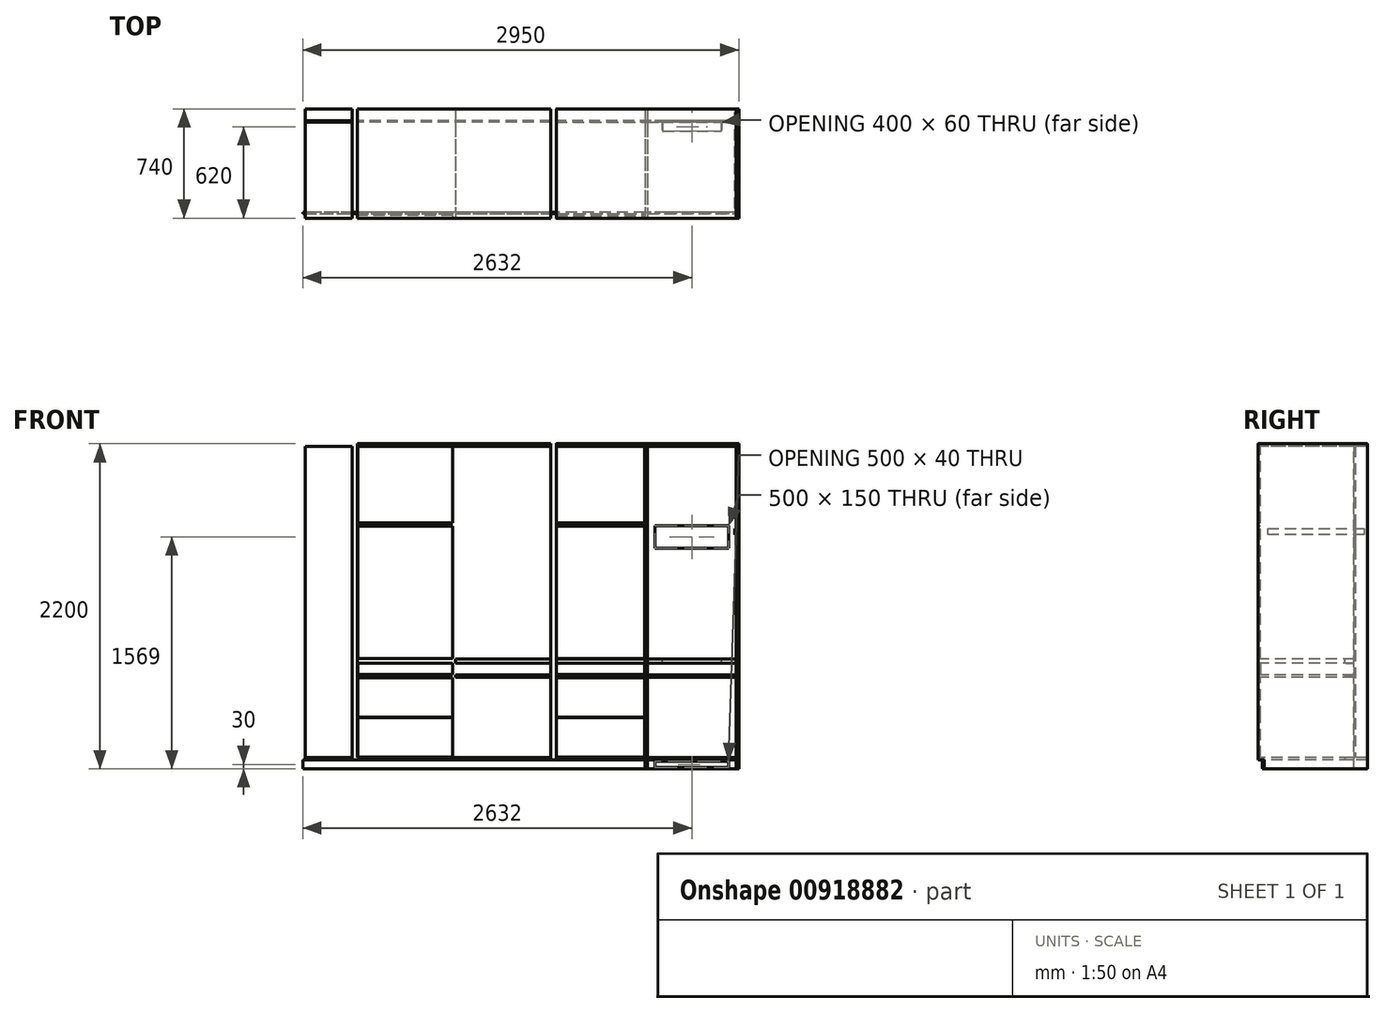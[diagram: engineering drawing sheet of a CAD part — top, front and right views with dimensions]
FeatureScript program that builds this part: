
annotation { "Feature Type Name" : "Feature", "Feature Type Description" : "" }
export const myFeature = defineFeature(function(context is Context, id is Id, definition is map)
    precondition{}
    {
        {
            var Q0;
            Q0=qCreatedBy(makeId("Front.planeOp"),FACE);
            var sketch = newSketch(context, id + "F0", { "sketchPlane" : qUnion([Q0])});
            skLineSegment(sketch, "E0.right", {"start": v(2950, 0) * mm, "end": v(2950, 2200) * mm});
            skLineSegment(sketch, "E1", {"start": v(1714, 2200) * mm, "end": v(1714, 0) * mm});
            skLineSegment(sketch, "E2", {"start": v(2332, 0) * mm, "end": v(2332, 2182) * mm});
            skLineSegment(sketch, "E3", {"start": v(1696, 0) * mm, "end": v(1696, 2200) * mm});
            skLineSegment(sketch, "E4", {"start": v(2932, 0) * mm, "end": v(2932, 2200) * mm});
            skLineSegment(sketch, "E5", {"start": v(2314, 0) * mm, "end": v(2314, 2182) * mm});
            skLineSegment(sketch, "E6", {"start": v(2932, 2200) * mm, "end": v(2950, 2200) * mm});
            skLineSegment(sketch, "E7", {"start": v(2932, 2200) * mm, "end": v(1714, 2200) * mm});
            skLineSegment(sketch, "E8", {"start": v(1714, 2182) * mm, "end": v(2932, 2182) * mm});
            skLineSegment(sketch, "E9", {"start": v(1714, 2200) * mm, "end": v(1696, 2200) * mm});
            skLineSegment(sketch, "E10", {"start": v(1714, 0) * mm, "end": v(1696, 0) * mm});
            skLineSegment(sketch, "E11", {"start": v(2932, 0) * mm, "end": v(2950, 0) * mm});
            skLineSegment(sketch, "E12", {"start": v(1714, 744) * mm, "end": v(2314, 744) * mm});
            skLineSegment(sketch, "E13", {"start": v(1714, 716) * mm, "end": v(2314, 716) * mm});
            skLineSegment(sketch, "E14", {"start": v(1714, 1662) * mm, "end": v(2314, 1662) * mm});
            skLineSegment(sketch, "E15", {"start": v(2932, 1644) * mm, "end": v(2332, 1644) * mm});
            skLineSegment(sketch, "E16.MirrorCS", {"start": v(1678, 2200) * mm, "end": v(1678, 0) * mm});
            skLineSegment(sketch, "E17.MirrorCS", {"start": v(1678, 2182) * mm, "end": v(370, 2182) * mm});
            skLineSegment(sketch, "E18.MirrorCS", {"start": v(370, 2200) * mm, "end": v(1678, 2200) * mm});
            skLineSegment(sketch, "E19.MirrorCS", {"start": v(1015, 0) * mm, "end": v(1015, 2182) * mm});
            skLineSegment(sketch, "E20.MirrorCS", {"start": v(1033, 0) * mm, "end": v(1033, 2182) * mm});
            skLineSegment(sketch, "E21.MirrorCS", {"start": v(370, 0) * mm, "end": v(370, 2200) * mm});
            skLineSegment(sketch, "E22.MirrorCS", {"start": v(1678, 0) * mm, "end": v(1696, 0) * mm});
            skLineSegment(sketch, "E23.MirrorCS", {"start": v(1678, 2200) * mm, "end": v(1696, 2200) * mm});
            skLineSegment(sketch, "E24", {"start": v(2932, 618) * mm, "end": v(2332, 618) * mm});
            skLineSegment(sketch, "E25", {"start": v(2332, 636) * mm, "end": v(2932, 636) * mm});
            skLineSegment(sketch, "E26", {"start": v(2314, 636) * mm, "end": v(1714, 636) * mm});
            skLineSegment(sketch, "E27", {"start": v(1714, 618) * mm, "end": v(2314, 618) * mm});
            skLineSegment(sketch, "E28", {"start": v(1678, 1644) * mm, "end": v(1033, 1644) * mm});
            skLineSegment(sketch, "E29", {"start": v(1678, 1662) * mm, "end": v(1033, 1662) * mm});
            skLineSegment(sketch, "E30", {"start": v(1678, 716) * mm, "end": v(1033, 716) * mm});
            skLineSegment(sketch, "E31", {"start": v(1015, 716) * mm, "end": v(370, 716) * mm});
            skLineSegment(sketch, "E32", {"start": v(1678, 618) * mm, "end": v(1033, 618) * mm});
            skLineSegment(sketch, "E33", {"start": v(1015, 618) * mm, "end": v(370, 618) * mm});
            skLineSegment(sketch, "E34", {"start": v(1678, 744) * mm, "end": v(1033, 744) * mm});
            skLineSegment(sketch, "E35", {"start": v(1015, 744) * mm, "end": v(370, 744) * mm});
            skLineSegment(sketch, "E36", {"start": v(1678, 636) * mm, "end": v(1033, 636) * mm});
            skLineSegment(sketch, "E37", {"start": v(1015, 636) * mm, "end": v(370, 636) * mm});
            skLineSegment(sketch, "E38", {"start": v(352, 2200) * mm, "end": v(352, 10) * mm});
            skLineSegment(sketch, "E39", {"start": v(334, 10) * mm, "end": v(334, 2200) * mm});
            skLineSegment(sketch, "E40", {"start": v(0, 2200) * mm, "end": v(334, 2200) * mm});
            skLineSegment(sketch, "E41", {"start": v(334, 2182) * mm, "end": v(18, 2182) * mm});
            skLineSegment(sketch, "E42", {"start": v(334, 2200) * mm, "end": v(352, 2200) * mm});
            skLineSegment(sketch, "E43", {"start": v(352, 10) * mm, "end": v(334, 10) * mm});
            skLineSegment(sketch, "E44", {"start": v(352, 10) * mm, "end": v(370, 10) * mm});
            skLineSegment(sketch, "E45", {"start": v(18, 2200) * mm, "end": v(18, 0) * mm});
            skLineSegment(sketch, "E46", {"start": v(0, 2200) * mm, "end": v(0, 0) * mm});
            skLineSegment(sketch, "E47.trimOffspring", {"start": v(2332, 744) * mm, "end": v(2932, 744) * mm});
            skLineSegment(sketch, "E48.trimOffspring", {"start": v(2332, 1662) * mm, "end": v(2932, 1662) * mm});
            skLineSegment(sketch, "E49.trimOffspring", {"start": v(2314, 1644) * mm, "end": v(1714, 1644) * mm});
            skLineSegment(sketch, "E50.trimOffspring", {"start": v(1015, 1662) * mm, "end": v(370, 1662) * mm});
            skLineSegment(sketch, "E51.trimOffspring", {"start": v(1015, 1644) * mm, "end": v(370, 1644) * mm});
            skLineSegment(sketch, "E52", {"start": v(2332, 716) * mm, "end": v(2932, 716) * mm});
            skLineSegment(sketch, "E53", {"start": v(2314, 0) * mm, "end": v(2332, 0) * mm});
            skLineSegment(sketch, "E54", {"start": v(1015, 0) * mm, "end": v(1033, 0) * mm});
            skLineSegment(sketch, "E55", {"start": v(0, 0) * mm, "end": v(18, 0) * mm});
            skLineSegment(sketch, "E56", {"start": v(2932, 60) * mm, "end": v(2332, 60) * mm});
            skLineSegment(sketch, "E57", {"start": v(2932, 78) * mm, "end": v(2332, 78) * mm});
            skLineSegment(sketch, "E58", {"start": v(2314, 60) * mm, "end": v(1714, 60) * mm});
            skLineSegment(sketch, "E59", {"start": v(2314, 78) * mm, "end": v(1714, 78) * mm});
            skLineSegment(sketch, "E60", {"start": v(1678, 78) * mm, "end": v(1033, 78) * mm});
            skLineSegment(sketch, "E61", {"start": v(1678, 60) * mm, "end": v(1033, 60) * mm});
            skLineSegment(sketch, "E62", {"start": v(1015, 78) * mm, "end": v(370, 78) * mm});
            skLineSegment(sketch, "E63", {"start": v(1015, 60) * mm, "end": v(370, 60) * mm});
            skLineSegment(sketch, "E64", {"start": v(334, 78) * mm, "end": v(18, 78) * mm});
            skLineSegment(sketch, "E65", {"start": v(334, 60) * mm, "end": v(18, 60) * mm});
            skLineSegment(sketch, "E66", {"start": v(352, 2200) * mm, "end": v(370, 2200) * mm});
            skSolve(sketch);
        }
        {
            var Q0;
            Q0=makeQuery(id+"F0.imprint","IMPRINT",FACE,{"disambiguationData":[TD([[makeQuery(id+"F0.imprint","IMPRINT",EDGE,{"derivedFrom":sQuery(id+"F0.wireOp",EDGE,"E0.right")}),1.0]])]});
            extrude(context, id + "F1", {"entities" : qUnion([Q0]), "oppositeDirection" : true, "depth" : 740 * mm, "offsetDistance" : 25 * mm});
        }
        {
            var Q0;
            {var subQ0=sQuery(id+"F0.wireOp",EDGE,"E24");Q0=makeQuery(id+"F0.imprint","IMPRINT",FACE,{"disambiguationData":[TD([[makeQuery(id+"F0.imprint","IMPRINT",EDGE,{"derivedFrom":subQ0}),-1.0]])]});}
            extrude(context, id + "F2", {"entities" : qUnion([Q0]), "oppositeDirection" : true, "depth" : 650 * mm, "offsetDistance" : 25 * mm});
        }
        {
            var Q0;
            {var subQ0=sQuery(id+"F0.wireOp",EDGE,"E47.trimOffspring");Q0=makeQuery(id+"F0.imprint","IMPRINT",FACE,{"disambiguationData":[TD([[makeQuery(id+"F0.imprint","IMPRINT",EDGE,{"derivedFrom":subQ0}),-1.0]])]});}
            extrude(context, id + "F3", {"entities" : qUnion([Q0]), "oppositeDirection" : true, "depth" : 650 * mm, "offsetDistance" : 25 * mm});
        }
        {
            var Q0;
            {var subQ4=sQuery(id+"F0.wireOp",EDGE,"E7");Q0=makeQuery(id+"F0.imprint","IMPRINT",FACE,{"disambiguationData":[TD([[makeQuery(id+"F0.imprint","IMPRINT",EDGE,{"derivedFrom":subQ4}),1.0]])]});}
            extrude(context, id + "F4", {"entities" : qUnion([Q0]), "oppositeDirection" : true, "depth" : 740 * mm, "offsetDistance" : 25 * mm});
        }
        {
            var Q0;
            {var subQ4=sQuery(id+"F0.wireOp",EDGE,"Y9ucpfED-vLSd-DeHG-6LsV-7PyXNKgOYs4r");var subQ7=sQuery(id+"F0.wireOp",EDGE,"E2");var subQ12=makeQuery(id+"F0.imprint","INTERSECT",VERTEX,{"derivedFrom":[subQ7,subQ4]});Q0=makeQuery(id+"F0.imprint","IMPRINT",FACE,{"disambiguationData":[TD([[makeQuery(id+"F0.imprint","IMPRINT",EDGE,{"disambiguationData":[TD([[subQ12,-1.0]])],"derivedFrom":subQ7}),1.0]])]});}
            extrude(context, id + "F5", {"entities" : qUnion([Q0]), "oppositeDirection" : true, "depth" : 650 * mm, "offsetDistance" : 25 * mm});
        }
        {
            var Q0;
            Q0=makeQuery(id+"F4.opExtrude","CAP_EDGE",EDGE,{"disambiguationData":[OSD([sQuery(id+"F0.wireOp",EDGE,"E7")])],"isStart":false});
            var Q1;
            Q1=makeQuery(id+"F4.opExtrude","SWEPT_EDGE",EDGE,{"disambiguationData":[OSD([sQuery(id+"F0.wireOp",EDGE,"E1"),sQuery(id+"F0.wireOp",EDGE,"E7"),sQuery(id+"F0.wireOp",EDGE,"E9")])]});
            var Q2;
            Q2=makeQuery(id+"F4.opExtrude","CAP_EDGE",EDGE,{"disambiguationData":[OSD([sQuery(id+"F0.wireOp",EDGE,"E8")])],"isStart":false});
            var Q3;
            Q3=makeQuery(id+"F4.opExtrude","SWEPT_EDGE",EDGE,{"disambiguationData":[OSD([sQuery(id+"F0.wireOp",EDGE,"E1"),sQuery(id+"F0.wireOp",EDGE,"E8")])]});
            var Q4;
            Q4=makeQuery(id+"F4.opExtrude","CAP_EDGE",EDGE,{"disambiguationData":[OSD([sQuery(id+"F0.wireOp",EDGE,"E7")])],"isStart":true});
            var Q5;
            Q5=makeQuery(id+"F4.opExtrude","CAP_EDGE",EDGE,{"disambiguationData":[OSD([sQuery(id+"F0.wireOp",EDGE,"E8")])],"isStart":true});
            var Q6;
            Q6=makeQuery(id+"F4.opExtrude","CAP_EDGE",EDGE,{"disambiguationData":[OSD([sQuery(id+"F0.wireOp",EDGE,"E1")])],"isStart":true});
            var Q7;
            Q7=makeQuery(id+"F4.opExtrude","CAP_EDGE",EDGE,{"disambiguationData":[OSD([sQuery(id+"F0.wireOp",EDGE,"E1")])],"isStart":false});
            var Q8;
            Q8=makeQuery(id+"F4.opExtrude","SWEPT_EDGE",EDGE,{"disambiguationData":[OSD([sQuery(id+"F0.wireOp",EDGE,"E4"),sQuery(id+"F0.wireOp",EDGE,"E6"),sQuery(id+"F0.wireOp",EDGE,"E7")])]});
            var Q9;
            Q9=makeQuery(id+"F4.opExtrude","CAP_EDGE",EDGE,{"disambiguationData":[OSD([sQuery(id+"F0.wireOp",EDGE,"E4")])],"isStart":false});
            var Q10;
            Q10=makeQuery(id+"F4.opExtrude","SWEPT_EDGE",EDGE,{"disambiguationData":[OSD([sQuery(id+"F0.wireOp",EDGE,"E4"),sQuery(id+"F0.wireOp",EDGE,"E8")])]});
            var Q11;
            Q11=makeQuery(id+"F4.opExtrude","CAP_EDGE",EDGE,{"disambiguationData":[OSD([sQuery(id+"F0.wireOp",EDGE,"E4")])],"isStart":true});
            fillet(context, id + "F6", {"entities" : qUnion([Q0, Q1, Q2, Q3, Q4, Q5, Q6, Q7, Q8, Q9, Q10, Q11]), "radius" : 2 * mm, "tangentPropagation" : true, "allowEdgeOverflow" : false});
        }
        {
            var Q0;
            Q0=makeQuery(id+"F1.opExtrude","SWEPT_EDGE",EDGE,{"disambiguationData":[OSD([sQuery(id+"F0.wireOp",EDGE,"E0.right"),sQuery(id+"F0.wireOp",EDGE,"E6")])]});
            var Q1;
            Q1=makeQuery(id+"F1.opExtrude","CAP_EDGE",EDGE,{"disambiguationData":[OSD([sQuery(id+"F0.wireOp",EDGE,"E6")])],"isStart":true});
            var Q2;
            Q2=makeQuery(id+"F1.opExtrude","CAP_EDGE",EDGE,{"disambiguationData":[OSD([sQuery(id+"F0.wireOp",EDGE,"E0.right")])],"isStart":true});
            var Q3;
            Q3=makeQuery(id+"F1.opExtrude","CAP_EDGE",EDGE,{"disambiguationData":[OSD([sQuery(id+"F0.wireOp",EDGE,"E4")])],"isStart":true});
            var Q4;
            Q4=makeQuery(id+"F1.opExtrude","SWEPT_EDGE",EDGE,{"disambiguationData":[OSD([sQuery(id+"F0.wireOp",EDGE,"E4"),sQuery(id+"F0.wireOp",EDGE,"E6"),sQuery(id+"F0.wireOp",EDGE,"E7")])]});
            var Q5;
            Q5=makeQuery(id+"F1.opExtrude","CAP_EDGE",EDGE,{"disambiguationData":[OSD([sQuery(id+"F0.wireOp",EDGE,"E0.right")])],"isStart":false});
            var Q6;
            Q6=makeQuery(id+"F1.opExtrude","CAP_EDGE",EDGE,{"disambiguationData":[OSD([sQuery(id+"F0.wireOp",EDGE,"E4")])],"isStart":false});
            var Q7;
            Q7=makeQuery(id+"F1.opExtrude","CAP_EDGE",EDGE,{"disambiguationData":[OSD([sQuery(id+"F0.wireOp",EDGE,"E6")])],"isStart":false});
            var Q8;
            Q8=makeQuery(id+"F1.opExtrude","CAP_EDGE",EDGE,{"disambiguationData":[OSD([sQuery(id+"F0.wireOp",EDGE,"E11")])],"isStart":false});
            var Q9;
            Q9=makeQuery(id+"F1.opExtrude","SWEPT_EDGE",EDGE,{"disambiguationData":[OSD([sQuery(id+"F0.wireOp",EDGE,"E0.right"),sQuery(id+"F0.wireOp",EDGE,"E11")])]});
            var Q10;
            Q10=makeQuery(id+"F1.opExtrude","SWEPT_EDGE",EDGE,{"disambiguationData":[OSD([sQuery(id+"F0.wireOp",EDGE,"E4"),sQuery(id+"F0.wireOp",EDGE,"AxWzxlak-ThEC-pPOV-fKd7-931bqLQH28Kv"),sQuery(id+"F0.wireOp",EDGE,"E11")])]});
            var Q11;
            Q11=makeQuery(id+"F1.opExtrude","CAP_EDGE",EDGE,{"disambiguationData":[OSD([sQuery(id+"F0.wireOp",EDGE,"E11")])],"isStart":true});
            var Q12;
            Q12=makeQuery(id+"F5.opExtrude","SWEPT_EDGE",EDGE,{"disambiguationData":[OSD([sQuery(id+"F0.wireOp",EDGE,"E2"),sQuery(id+"F0.wireOp",EDGE,"Y9ucpfED-vLSd-DeHG-6LsV-7PyXNKgOYs4r")])]});
            var Q13;
            Q13=makeQuery(id+"F5.opExtrude","CAP_EDGE",EDGE,{"disambiguationData":[OSD([sQuery(id+"F0.wireOp",EDGE,"Y9ucpfED-vLSd-DeHG-6LsV-7PyXNKgOYs4r")])],"isStart":true});
            var Q14;
            Q14=makeQuery(id+"F5.opExtrude","CAP_EDGE",EDGE,{"disambiguationData":[OSD([sQuery(id+"F0.wireOp",EDGE,"E5")])],"isStart":true});
            var Q15;
            Q15=makeQuery(id+"F5.opExtrude","SWEPT_EDGE",EDGE,{"disambiguationData":[OSD([sQuery(id+"F0.wireOp",EDGE,"E5"),sQuery(id+"F0.wireOp",EDGE,"Y9ucpfED-vLSd-DeHG-6LsV-7PyXNKgOYs4r")])]});
            var Q16;
            Q16=makeQuery(id+"F5.opExtrude","CAP_EDGE",EDGE,{"disambiguationData":[OSD([sQuery(id+"F0.wireOp",EDGE,"E2")])],"isStart":true});
            var Q17;
            Q17=makeQuery(id+"F5.opExtrude","CAP_EDGE",EDGE,{"disambiguationData":[OSD([sQuery(id+"F0.wireOp",EDGE,"Y9ucpfED-vLSd-DeHG-6LsV-7PyXNKgOYs4r")])],"isStart":false});
            var Q18;
            Q18=makeQuery(id+"F5.opExtrude","CAP_EDGE",EDGE,{"disambiguationData":[OSD([sQuery(id+"F0.wireOp",EDGE,"E5")])],"isStart":false});
            var Q19;
            Q19=makeQuery(id+"F5.opExtrude","CAP_EDGE",EDGE,{"disambiguationData":[OSD([sQuery(id+"F0.wireOp",EDGE,"E2")])],"isStart":false});
            var Q20;
            Q20=makeQuery(id+"F5.opExtrude","CAP_EDGE",EDGE,{"disambiguationData":[OSD([sQuery(id+"F0.wireOp",EDGE,"E8")])],"isStart":false});
            var Q21;
            Q21=makeQuery(id+"F5.opExtrude","SWEPT_EDGE",EDGE,{"disambiguationData":[OSD([sQuery(id+"F0.wireOp",EDGE,"E5"),sQuery(id+"F0.wireOp",EDGE,"E8")])]});
            var Q22;
            Q22=makeQuery(id+"F5.opExtrude","SWEPT_EDGE",EDGE,{"disambiguationData":[OSD([sQuery(id+"F0.wireOp",EDGE,"E2"),sQuery(id+"F0.wireOp",EDGE,"E8")])]});
            var Q23;
            Q23=makeQuery(id+"F5.opExtrude","CAP_EDGE",EDGE,{"disambiguationData":[OSD([sQuery(id+"F0.wireOp",EDGE,"E8")])],"isStart":true});
            fillet(context, id + "F7", {"entities" : qUnion([Q0, Q1, Q2, Q3, Q4, Q5, Q6, Q7, Q8, Q9, Q10, Q11, Q12, Q13, Q14, Q15, Q16, Q17, Q18, Q19, Q20, Q21, Q22, Q23]), "radius" : 2 * mm, "tangentPropagation" : true, "allowEdgeOverflow" : false});
        }
        {
            var Q0;
            Q0=makeQuery(id+"F2.opExtrude","CAP_EDGE",EDGE,{"disambiguationData":[OSD([sQuery(id+"F0.wireOp",EDGE,"E24")])],"isStart":true});
            var Q1;
            Q1=makeQuery(id+"F2.opExtrude","CAP_EDGE",EDGE,{"disambiguationData":[OSD([sQuery(id+"F0.wireOp",EDGE,"E25")])],"isStart":true});
            var Q2;
            Q2=makeQuery(id+"F2.opExtrude","CAP_EDGE",EDGE,{"disambiguationData":[OSD([sQuery(id+"F0.wireOp",EDGE,"E2")])],"isStart":true});
            var Q3;
            Q3=makeQuery(id+"F2.opExtrude","SWEPT_EDGE",EDGE,{"disambiguationData":[OSD([sQuery(id+"F0.wireOp",EDGE,"E2"),sQuery(id+"F0.wireOp",EDGE,"E25")])]});
            var Q4;
            Q4=makeQuery(id+"F2.opExtrude","SWEPT_EDGE",EDGE,{"disambiguationData":[OSD([sQuery(id+"F0.wireOp",EDGE,"E2"),sQuery(id+"F0.wireOp",EDGE,"E24")])]});
            var Q5;
            Q5=makeQuery(id+"F2.opExtrude","CAP_EDGE",EDGE,{"disambiguationData":[OSD([sQuery(id+"F0.wireOp",EDGE,"E25")])],"isStart":false});
            var Q6;
            Q6=makeQuery(id+"F2.opExtrude","CAP_EDGE",EDGE,{"disambiguationData":[OSD([sQuery(id+"F0.wireOp",EDGE,"E24")])],"isStart":false});
            var Q7;
            Q7=makeQuery(id+"F2.opExtrude","CAP_EDGE",EDGE,{"disambiguationData":[OSD([sQuery(id+"F0.wireOp",EDGE,"E2")])],"isStart":false});
            var Q8;
            Q8=makeQuery(id+"F2.opExtrude","SWEPT_EDGE",EDGE,{"disambiguationData":[OSD([sQuery(id+"F0.wireOp",EDGE,"E4"),sQuery(id+"F0.wireOp",EDGE,"E25")])]});
            var Q9;
            Q9=makeQuery(id+"F2.opExtrude","CAP_EDGE",EDGE,{"disambiguationData":[OSD([sQuery(id+"F0.wireOp",EDGE,"E4")])],"isStart":false});
            var Q10;
            Q10=makeQuery(id+"F2.opExtrude","SWEPT_EDGE",EDGE,{"disambiguationData":[OSD([sQuery(id+"F0.wireOp",EDGE,"E4"),sQuery(id+"F0.wireOp",EDGE,"E24")])]});
            var Q11;
            Q11=makeQuery(id+"F2.opExtrude","CAP_EDGE",EDGE,{"disambiguationData":[OSD([sQuery(id+"F0.wireOp",EDGE,"E4")])],"isStart":true});
            fillet(context, id + "F8", {"entities" : qUnion([Q0, Q1, Q2, Q3, Q4, Q5, Q6, Q7, Q8, Q9, Q10, Q11]), "radius" : 2 * mm, "tangentPropagation" : true, "allowEdgeOverflow" : false});
        }
        {
            var Q0;
            Q0=makeQuery(id+"F3.opExtrude","SWEPT_FACE",FACE,{"disambiguationData":[OSD([sQuery(id+"F0.wireOp",EDGE,"E4")])]});
            var Q1;
            Q1=makeQuery(id+"F3.opExtrude","SWEPT_FACE",FACE,{"disambiguationData":[OSD([sQuery(id+"F0.wireOp",EDGE,"E2")])]});
            var Q2;
            Q2=makeQuery(id+"F3.opExtrude","CAP_FACE",FACE,{"disambiguationData":[OSD([sQuery(id+"F0.wireOp",EDGE,"E2"),sQuery(id+"F0.wireOp",EDGE,"E4"),sQuery(id+"F0.wireOp",EDGE,"E47.trimOffspring"),sQuery(id+"F0.wireOp",EDGE,"576773fe-4976-4b42-a3d9-79eeba28c3bd.trimOffspring")])],"isStart":true});
            fillet(context, id + "F9", {"entities" : qUnion([Q0, Q1, Q2]), "radius" : 2 * mm, "tangentPropagation" : true, "allowEdgeOverflow" : false});
        }
        {
            var Q0;
            {var subQ0=sQuery(id+"F0.wireOp",EDGE,"E64");Q0=makeQuery(id+"F0.imprint","IMPRINT",FACE,{"disambiguationData":[TD([[makeQuery(id+"F0.imprint","IMPRINT",EDGE,{"derivedFrom":subQ0}),1.0]])]});}
            extrude(context, id + "F10", {"entities" : qUnion([Q0]), "oppositeDirection" : true, "depth" : 740 * mm, "offsetDistance" : 25 * mm});
        }
        {
            var Q0;
            {var subQ0=sQuery(id+"F0.wireOp",EDGE,"E56");Q0=makeQuery(id+"F0.imprint","IMPRINT",FACE,{"disambiguationData":[TD([[makeQuery(id+"F0.imprint","IMPRINT",EDGE,{"derivedFrom":subQ0}),-1.0]])]});}
            extrude(context, id + "F11", {"entities" : qUnion([Q0]), "oppositeDirection" : true, "depth" : 740 * mm, "offsetDistance" : 25 * mm});
        }
        {
            var Q0;
            {var subQ0=sQuery(id+"F0.wireOp",EDGE,"E26");Q0=makeQuery(id+"F0.imprint","IMPRINT",FACE,{"disambiguationData":[TD([[makeQuery(id+"F0.imprint","IMPRINT",EDGE,{"derivedFrom":subQ0}),1.0]])]});}
            extrude(context, id + "F12", {"entities" : qUnion([Q0]), "oppositeDirection" : true, "depth" : 650 * mm, "offsetDistance" : 25 * mm});
        }
        {
            var Q0;
            Q0=qCreatedBy(makeId("Top.planeOp"),FACE);
            var sketch = newSketch(context, id + "F13", { "sketchPlane" : qUnion([Q0])});
            skLineSegment(sketch, "E67", {"start": v(0, 30) * mm, "end": v(3102.92, 30) * mm, "construction": true});
            skLineSegment(sketch, "E68.0", {"start": v(352, 0) * mm, "end": v(334, 0) * mm});
            skLineSegment(sketch, "E69.0", {"start": v(352, 0) * mm, "end": v(370, 0) * mm});
            skLineSegment(sketch, "E70.0", {"start": v(1015, 0) * mm, "end": v(1033, 0) * mm});
            skLineSegment(sketch, "E71.0", {"start": v(1678, 0) * mm, "end": v(1696, 0) * mm});
            skLineSegment(sketch, "E72.0", {"start": v(1714, 0) * mm, "end": v(1696, 0) * mm});
            skLineSegment(sketch, "E73.0", {"start": v(2314, 0) * mm, "end": v(2332, 0) * mm});
            skLineSegment(sketch, "E74.0", {"start": v(2932, 0) * mm, "end": v(2950, 0) * mm});
            skLineSegment(sketch, "E75", {"start": v(0, 30) * mm, "end": v(334, 30) * mm});
            skLineSegment(sketch, "E76", {"start": v(370, 42) * mm, "end": v(0, 42) * mm});
            skLineSegment(sketch, "E77", {"start": v(370, 30) * mm, "end": v(2332, 30) * mm});
            skLineSegment(sketch, "E78", {"start": v(2332, 42) * mm, "end": v(370, 42) * mm});
            skLineSegment(sketch, "E79", {"start": v(2332, 30) * mm, "end": v(2932, 30) * mm});
            skLineSegment(sketch, "E80", {"start": v(2914, 42) * mm, "end": v(2332, 42) * mm});
            skLineSegment(sketch, "E81", {"start": v(334, 30) * mm, "end": v(370, 30) * mm});
            skLineSegment(sketch, "E82.0", {"start": v(2950, 2) * mm, "end": v(2950, 738) * mm});
            skLineSegment(sketch, "E83", {"start": v(2932, 30) * mm, "end": v(2950, 30) * mm});
            skLineSegment(sketch, "E84", {"start": v(2950, 30) * mm, "end": v(2950, 42) * mm});
            skLineSegment(sketch, "E85", {"start": v(2950, 42) * mm, "end": v(2914, 42) * mm});
            skLineSegment(sketch, "E86", {"start": v(0, 42) * mm, "end": v(0, 30) * mm});
            skLineSegment(sketch, "E87", {"start": v(0, 30) * mm, "end": v(0, 30) * mm});
            skSolve(sketch);
        }
        {
            var Q0;
            Q0 = qSketchRegion(id + "F13", true);
            var Q1;
            Q1=makeQuery(id+"F10.opExtrude","SWEPT_FACE",FACE,{"disambiguationData":[OSD([sQuery(id+"F0.wireOp",EDGE,"E65")])]});
            extrude(context, id + "F14", {"entities" : qUnion([Q0]), "endBound" : BoundingType.UP_TO_SURFACE, "depth" : 25 * mm, "endBoundEntityFace" : qUnion([Q1]), "offsetDistance" : 25 * mm});
        }
        {
            var Q0;
            Q0=makeQuery(id+"F14.opExtrude","SWEPT_FACE",FACE,{"disambiguationData":[OSD([sQuery(id+"F13.wireOp",EDGE,"E79")])]});
            var sketch = newSketch(context, id + "F15", { "sketchPlane" : qUnion([Q0])});
            skLineSegment(sketch, "E88", {"start": v(2387, 50) * mm, "end": v(2877, 50) * mm});
            skLineSegment(sketch, "E89", {"start": v(2882, 45) * mm, "end": v(2882, 15) * mm});
            skLineSegment(sketch, "E90", {"start": v(2877, 10) * mm, "end": v(2387, 10) * mm});
            skLineSegment(sketch, "E91", {"start": v(2382, 15) * mm, "end": v(2382, 45) * mm});
            skPoint(sketch, "E92.visualSharp", {"position": v(2382, 50) * mm});
            skArc(sketch, "E92.filletArc", {"start": v(2387, 50) * mm, "mid": v(2383.46, 48.54) * mm, "end": v(2382, 45) * mm});
            skPoint(sketch, "E93.visualSharp", {"position": v(2382, 10) * mm});
            skArc(sketch, "E93.filletArc", {"start": v(2382, 15) * mm, "mid": v(2383.46, 11.46) * mm, "end": v(2387, 10) * mm});
            skPoint(sketch, "E94.visualSharp", {"position": v(2882, 50) * mm});
            skArc(sketch, "E94.filletArc", {"start": v(2882, 45) * mm, "mid": v(2880.54, 48.54) * mm, "end": v(2877, 50) * mm});
            skPoint(sketch, "E95.visualSharp", {"position": v(2882, 10) * mm});
            skArc(sketch, "E95.filletArc", {"start": v(2877, 10) * mm, "mid": v(2880.54, 11.46) * mm, "end": v(2882, 15) * mm});
            skPoint(sketch, "E96", {"position": v(2632, 10) * mm});
            skLineSegment(sketch, "E97", {"start": v(2632, 0) * mm, "end": v(2632, 100.17) * mm, "construction": true});
            skPoint(sketch, "E98", {"position": v(2382, 30) * mm});
            skLineSegment(sketch, "E99", {"start": v(2535.58, 30) * mm, "end": v(2935.92, 30) * mm, "construction": true});
            skSolve(sketch);
        }
        {
            var Q0;
            Q0=makeQuery(id+"F15.imprint","IMPRINT",FACE,{"disambiguationData":[TD([[makeQuery(id+"F15.imprint","IMPRINT",EDGE,{"derivedFrom":sQuery(id+"F15.wireOp",EDGE,"E88")}),-1.0]])]});
            extrude(context, id + "F16", {"entities" : qUnion([Q0]), "operationType" : NewBodyOperationType.REMOVE, "oppositeDirection" : true, "depth" : 25 * mm, "offsetDistance" : 25 * mm});
        }
        {
            var Q0;
            Q0=makeQuery(id+"F3.opExtrude","SWEPT_FACE",FACE,{"disambiguationData":[OSD([sQuery(id+"F0.wireOp",EDGE,"E47.trimOffspring")])]});
            var sketch = newSketch(context, id + "F17", { "sketchPlane" : qUnion([Q0])});
            skLineSegment(sketch, "E100", {"start": v(2827, 590) * mm, "end": v(2437, 590) * mm});
            skLineSegment(sketch, "E101", {"start": v(2432, 595) * mm, "end": v(2432, 650) * mm});
            skLineSegment(sketch, "E102", {"start": v(2832, 650) * mm, "end": v(2832, 595) * mm});
            skLineSegment(sketch, "E103", {"start": v(2632, 650) * mm, "end": v(2632, 573.01) * mm, "construction": true});
            skPoint(sketch, "E104.visualSharp", {"position": v(2832, 590) * mm});
            skArc(sketch, "E104.filletArc", {"start": v(2827, 590) * mm, "mid": v(2830.54, 591.46) * mm, "end": v(2832, 595) * mm});
            skPoint(sketch, "E105.visualSharp", {"position": v(2432, 590) * mm});
            skArc(sketch, "E105.filletArc", {"start": v(2432, 595) * mm, "mid": v(2433.46, 591.46) * mm, "end": v(2437, 590) * mm});
            skLineSegment(sketch, "E106", {"start": v(2832, 650) * mm, "end": v(2432, 650) * mm});
            skLineSegment(sketch, "E107.0", {"start": v(2334, 650) * mm, "end": v(2930, 650) * mm});
            skSolve(sketch);
        }
        {
            var Q0;
            Q0=makeQuery(id+"F17.imprint","IMPRINT",FACE,{"disambiguationData":[TD([[makeQuery(id+"F17.imprint","IMPRINT",EDGE,{"derivedFrom":sQuery(id+"F17.wireOp",EDGE,"E100")}),-1.0]])]});
            extrude(context, id + "F18", {"entities" : qUnion([Q0]), "operationType" : NewBodyOperationType.REMOVE, "endBound" : BoundingType.THROUGH_ALL, "oppositeDirection" : true, "depth" : 25 * mm, "offsetDistance" : 25 * mm});
        }
        {
            var Q0;
            {var subQ5=sQuery(id+"F0.wireOp",EDGE,"E18.MirrorCS");Q0=makeQuery(id+"F0.imprint","IMPRINT",FACE,{"disambiguationData":[TD([[makeQuery(id+"F0.imprint","IMPRINT",EDGE,{"derivedFrom":subQ5}),-1.0]])]});}
            extrude(context, id + "F19", {"entities" : qUnion([Q0]), "oppositeDirection" : true, "depth" : 740 * mm, "offsetDistance" : 25 * mm});
        }
        {
            var Q0;
            {var subQ0=sQuery(id+"F0.wireOp",EDGE,"E58");Q0=makeQuery(id+"F0.imprint","IMPRINT",FACE,{"disambiguationData":[TD([[makeQuery(id+"F0.imprint","IMPRINT",EDGE,{"derivedFrom":subQ0}),-1.0]])]});}
            extrude(context, id + "F20", {"entities" : qUnion([Q0]), "oppositeDirection" : true, "depth" : 740 * mm, "offsetDistance" : 25 * mm});
        }
        {
            var Q0;
            {var subQ0=sQuery(id+"F0.wireOp",EDGE,"E12");Q0=makeQuery(id+"F0.imprint","IMPRINT",FACE,{"disambiguationData":[TD([[makeQuery(id+"F0.imprint","IMPRINT",EDGE,{"derivedFrom":subQ0}),-1.0]])]});}
            extrude(context, id + "F21", {"entities" : qUnion([Q0]), "oppositeDirection" : true, "depth" : 650 * mm, "offsetDistance" : 25 * mm});
        }
        {
            var Q0;
            Q0=makeQuery(id+"F5.opExtrude","CAP_FACE",FACE,{"disambiguationData":[OSD([sQuery(id+"F0.wireOp",EDGE,"E2"),sQuery(id+"F0.wireOp",EDGE,"E5"),sQuery(id+"F0.wireOp",EDGE,"E8"),sQuery(id+"F0.wireOp",EDGE,"E53")])],"isStart":false});
            var sketch = newSketch(context, id + "F22", { "sketchPlane" : qUnion([Q0])});
            skLineSegment(sketch, "E108.0", {"start": v(-1714, 2182) * mm, "end": v(-2932, 2182) * mm});
            skLineSegment(sketch, "E109.0", {"start": v(-2932, 0) * mm, "end": v(-2932, 2200) * mm});
            skLineSegment(sketch, "E110.0", {"start": v(-1714, 2200) * mm, "end": v(-1714, 0) * mm});
            skLineSegment(sketch, "E111.0", {"start": v(-2314, 78) * mm, "end": v(-1714, 78) * mm});
            skLineSegment(sketch, "E112.0", {"start": v(-2932, 78) * mm, "end": v(-2332, 78) * mm});
            skLineSegment(sketch, "E113.0", {"start": v(-1678, 2182) * mm, "end": v(-370, 2182) * mm});
            skLineSegment(sketch, "E114.0", {"start": v(-1678, 2200) * mm, "end": v(-1678, 0) * mm});
            skLineSegment(sketch, "E115.0", {"start": v(-370, 0) * mm, "end": v(-370, 2200) * mm});
            skLineSegment(sketch, "E116.0", {"start": v(-334, 10) * mm, "end": v(-334, 2200) * mm});
            skLineSegment(sketch, "E117.0", {"start": v(-334, 2182) * mm, "end": v(-18, 2182) * mm});
            skLineSegment(sketch, "E118.0", {"start": v(-18, 2200) * mm, "end": v(-18, 0) * mm});
            skLineSegment(sketch, "E119.0", {"start": v(-334, 78) * mm, "end": v(-18, 78) * mm});
            skLineSegment(sketch, "E120.0", {"start": v(-1015, 78) * mm, "end": v(-370, 78) * mm});
            skLineSegment(sketch, "E121.0", {"start": v(-1678, 78) * mm, "end": v(-1033, 78) * mm});
            skLineSegment(sketch, "E122.bottom", {"start": v(-2932, 2182) * mm, "end": v(-1714, 2182) * mm});
            skLineSegment(sketch, "E122.top", {"start": v(-2932, 78) * mm, "end": v(-1714, 78) * mm});
            skLineSegment(sketch, "E122.left", {"start": v(-2932, 2182) * mm, "end": v(-2932, 78) * mm});
            skLineSegment(sketch, "E122.right", {"start": v(-1714, 2182) * mm, "end": v(-1714, 78) * mm});
            skLineSegment(sketch, "E123.top", {"start": v(-1678, 78) * mm, "end": v(-370, 78) * mm});
            skLineSegment(sketch, "E123.left", {"start": v(-1678, 2182) * mm, "end": v(-1678, 78) * mm});
            skLineSegment(sketch, "E123.right", {"start": v(-370, 2182) * mm, "end": v(-370, 78) * mm});
            skLineSegment(sketch, "E124.left", {"start": v(-334, 2182) * mm, "end": v(-334, 78) * mm});
            skLineSegment(sketch, "E124.right", {"start": v(-18, 2182) * mm, "end": v(-18, 78) * mm});
            skLineSegment(sketch, "E125.0", {"start": v(-2932, 1644) * mm, "end": v(-2332, 1644) * mm});
            skLineSegment(sketch, "E126", {"start": v(-2882, 1644) * mm, "end": v(-2882, 1494) * mm});
            skLineSegment(sketch, "E127", {"start": v(-2882, 1494) * mm, "end": v(-2382, 1494) * mm});
            skLineSegment(sketch, "E128", {"start": v(-2382, 1494) * mm, "end": v(-2382, 1644) * mm});
            skLineSegment(sketch, "E129", {"start": v(-2632, 1644) * mm, "end": v(-2632, 1448.7) * mm, "construction": true});
            skSolve(sketch);
        }
        {
            var Q0;
            Q0 = qSketchRegion(id + "F22", true);
            extrude(context, id + "F23", {"entities" : qUnion([Q0]), "depth" : 9 * mm, "offsetDistance" : 25 * mm});
        }
        {
            var Q0;
            {var subQ0=sQuery(id+"F22.wireOp",EDGE,"E126");Q0=makeQuery(id+"F22.imprint","IMPRINT",FACE,{"disambiguationData":[TD([[makeQuery(id+"F22.imprint","IMPRINT",EDGE,{"derivedFrom":subQ0}),1.0]])]});}
            extrude(context, id + "F24", {"entities" : qUnion([Q0]), "operationType" : NewBodyOperationType.REMOVE, "oppositeDirection" : true, "depth" : 25 * mm, "offsetDistance" : 25 * mm});
        }
        {
            var Q0;
            {var subQ0=sQuery(id+"F0.wireOp",EDGE,"E30");Q0=makeQuery(id+"F0.imprint","IMPRINT",FACE,{"disambiguationData":[TD([[makeQuery(id+"F0.imprint","IMPRINT",EDGE,{"derivedFrom":subQ0}),-1.0]])]});}
            extrude(context, id + "F25", {"entities" : qUnion([Q0]), "oppositeDirection" : true, "depth" : 650 * mm, "offsetDistance" : 25 * mm});
        }
        {
            var Q0;
            {var subQ0=sQuery(id+"F0.wireOp",EDGE,"E32");Q0=makeQuery(id+"F0.imprint","IMPRINT",FACE,{"disambiguationData":[TD([[makeQuery(id+"F0.imprint","IMPRINT",EDGE,{"derivedFrom":subQ0}),-1.0]])]});}
            extrude(context, id + "F26", {"entities" : qUnion([Q0]), "oppositeDirection" : true, "depth" : 650 * mm, "offsetDistance" : 25 * mm});
        }
        {
            var Q0;
            {var subQ0=sQuery(id+"F0.wireOp",EDGE,"E60");Q0=makeQuery(id+"F0.imprint","IMPRINT",FACE,{"disambiguationData":[TD([[makeQuery(id+"F0.imprint","IMPRINT",EDGE,{"derivedFrom":subQ0}),1.0]])]});}
            extrude(context, id + "F27", {"entities" : qUnion([Q0]), "oppositeDirection" : true, "depth" : 740 * mm, "offsetDistance" : 25 * mm});
        }
        {
            var Q0;
            Q0=qCreatedBy(makeId("Front.planeOp"),FACE);
            var sketch = newSketch(context, id + "F28", { "sketchPlane" : qUnion([Q0])});
            skLineSegment(sketch, "E130.0", {"start": v(1015, 1644) * mm, "end": v(370, 1644) * mm, "construction": true});
            skLineSegment(sketch, "E131.0", {"start": v(370, 0) * mm, "end": v(370, 2200) * mm, "construction": true});
            skLineSegment(sketch, "E132.0", {"start": v(1015, 0) * mm, "end": v(1015, 2182) * mm, "construction": true});
            skLineSegment(sketch, "E133.0", {"start": v(1015, 744) * mm, "end": v(370, 744) * mm, "construction": true});
            skLineSegment(sketch, "E134.0", {"start": v(1015, 1642) * mm, "end": v(370, 1642) * mm});
            skLineSegment(sketch, "E135.0", {"start": v(372, 0) * mm, "end": v(372, 2200) * mm});
            skLineSegment(sketch, "E136.0", {"start": v(1015, 746) * mm, "end": v(372, 746) * mm});
            skLineSegment(sketch, "E137.0", {"start": v(1013, 0) * mm, "end": v(1013, 2182) * mm});
            skLineSegment(sketch, "E138.0", {"start": v(1015, 716) * mm, "end": v(370, 716) * mm, "construction": true});
            skLineSegment(sketch, "E139.0", {"start": v(1015, 636) * mm, "end": v(370, 636) * mm, "construction": true});
            skLineSegment(sketch, "E140.0", {"start": v(1015, 618) * mm, "end": v(370, 618) * mm, "construction": true});
            skLineSegment(sketch, "E141.0", {"start": v(1015, 78) * mm, "end": v(370, 78) * mm, "construction": true});
            skLineSegment(sketch, "E142.0", {"start": v(1015, 1662) * mm, "end": v(370, 1662) * mm, "construction": true});
            skLineSegment(sketch, "E143.0", {"start": v(1678, 2182) * mm, "end": v(370, 2182) * mm, "construction": true});
            skLineSegment(sketch, "E144.0", {"start": v(334, 2182) * mm, "end": v(18, 2182) * mm, "construction": true});
            skLineSegment(sketch, "E145.0", {"start": v(18, 2200) * mm, "end": v(18, 0) * mm, "construction": true});
            skLineSegment(sketch, "E146.0", {"start": v(334, 10) * mm, "end": v(334, 2200) * mm, "construction": true});
            skLineSegment(sketch, "E147.0", {"start": v(334, 78) * mm, "end": v(18, 78) * mm, "construction": true});
            skLineSegment(sketch, "E148.0", {"start": v(1714, 1662) * mm, "end": v(2314, 1662) * mm, "construction": true});
            skLineSegment(sketch, "E149.0", {"start": v(1714, 2200) * mm, "end": v(1714, 0) * mm, "construction": true});
            skLineSegment(sketch, "E150.0", {"start": v(2314, 0) * mm, "end": v(2314, 2182) * mm, "construction": true});
            skLineSegment(sketch, "E151.0", {"start": v(1714, 2182) * mm, "end": v(2932, 2182) * mm, "construction": true});
            skLineSegment(sketch, "E152.0", {"start": v(2314, 1644) * mm, "end": v(1714, 1644) * mm, "construction": true});
            skLineSegment(sketch, "E153.0", {"start": v(1714, 744) * mm, "end": v(2314, 744) * mm, "construction": true});
            skLineSegment(sketch, "E154.0", {"start": v(1714, 716) * mm, "end": v(2314, 716) * mm, "construction": true});
            skLineSegment(sketch, "E155.0", {"start": v(2314, 636) * mm, "end": v(1714, 636) * mm, "construction": true});
            skLineSegment(sketch, "E156.0", {"start": v(1714, 618) * mm, "end": v(2314, 618) * mm, "construction": true});
            skLineSegment(sketch, "E157.0", {"start": v(2314, 78) * mm, "end": v(1714, 78) * mm, "construction": true});
            skLineSegment(sketch, "E158.0", {"start": v(1015, 80) * mm, "end": v(370, 80) * mm});
            skLineSegment(sketch, "E159.0", {"start": v(1015, 616) * mm, "end": v(370, 616) * mm});
            skLineSegment(sketch, "E160", {"start": v(372, 348) * mm, "end": v(1013, 348) * mm, "construction": true});
            skLineSegment(sketch, "E161.0", {"start": v(372, 346) * mm, "end": v(1013, 346) * mm});
            skLineSegment(sketch, "E162.0", {"start": v(372, 350) * mm, "end": v(1013, 350) * mm});
            skLineSegment(sketch, "E163.0", {"start": v(1015, 714) * mm, "end": v(370, 714) * mm});
            skLineSegment(sketch, "E164.0", {"start": v(1015, 638) * mm, "end": v(370, 638) * mm});
            skLineSegment(sketch, "E165.0", {"start": v(1678, 2180) * mm, "end": v(370, 2180) * mm});
            skLineSegment(sketch, "E166.0", {"start": v(1015, 1664) * mm, "end": v(370, 1664) * mm});
            skLineSegment(sketch, "E167.0", {"start": v(1716, 2200) * mm, "end": v(1716, 0) * mm});
            skLineSegment(sketch, "E168.0", {"start": v(2312, 0) * mm, "end": v(2312, 2182) * mm});
            skLineSegment(sketch, "E169.0", {"start": v(1714, 1664) * mm, "end": v(2314, 1664) * mm});
            skLineSegment(sketch, "E170.0", {"start": v(1714, 2180) * mm, "end": v(2932, 2180) * mm});
            skLineSegment(sketch, "E171.0", {"start": v(2314, 1642) * mm, "end": v(1714, 1642) * mm});
            skLineSegment(sketch, "E172.0", {"start": v(1714, 746) * mm, "end": v(2314, 746) * mm});
            skLineSegment(sketch, "E173.0", {"start": v(1714, 714) * mm, "end": v(2314, 714) * mm});
            skLineSegment(sketch, "E174.0", {"start": v(2314, 638) * mm, "end": v(1714, 638) * mm});
            skLineSegment(sketch, "E175.0", {"start": v(1714, 616) * mm, "end": v(2314, 616) * mm});
            skLineSegment(sketch, "E176.0", {"start": v(2314, 80) * mm, "end": v(1714, 80) * mm});
            skLineSegment(sketch, "E177", {"start": v(1716, 348) * mm, "end": v(2312, 348) * mm, "construction": true});
            skLineSegment(sketch, "E178.0", {"start": v(1716, 346) * mm, "end": v(2312, 346) * mm});
            skLineSegment(sketch, "E179.0", {"start": v(1716, 350) * mm, "end": v(2312, 350) * mm});
            skSolve(sketch);
        }
        {
            var Q0;
            {var subQ0=sQuery(id+"F28.wireOp",EDGE,"E135.0");var subQ1=sQuery(id+"F28.wireOp",EDGE,"E134.0");var subQ2=makeQuery(id+"F28.imprint","INTERSECT",VERTEX,{"derivedFrom":[subQ1,subQ0]});Q0=makeQuery(id+"F28.imprint","IMPRINT",FACE,{"disambiguationData":[TD([[makeQuery(id+"F28.imprint","IMPRINT",EDGE,{"disambiguationData":[TD([[subQ2,1.0]])],"derivedFrom":subQ1}),1.0]])]});}
            var Q1;
            {var subQ0=sQuery(id+"F28.wireOp",EDGE,"E165.0");var subQ1=sQuery(id+"F28.wireOp",EDGE,"E135.0");var subQ2=makeQuery(id+"F28.imprint","INTERSECT",VERTEX,{"derivedFrom":[subQ1,subQ0]});Q1=makeQuery(id+"F28.imprint","IMPRINT",FACE,{"disambiguationData":[TD([[makeQuery(id+"F28.imprint","IMPRINT",EDGE,{"disambiguationData":[TD([[subQ2,1.0]])],"derivedFrom":subQ1}),-1.0]])]});}
            var Q2;
            {var subQ0=sQuery(id+"F28.wireOp",EDGE,"E164.0");var subQ1=sQuery(id+"F28.wireOp",EDGE,"E135.0");var subQ2=makeQuery(id+"F28.imprint","INTERSECT",VERTEX,{"derivedFrom":[subQ1,subQ0]});Q2=makeQuery(id+"F28.imprint","IMPRINT",FACE,{"disambiguationData":[TD([[makeQuery(id+"F28.imprint","IMPRINT",EDGE,{"disambiguationData":[TD([[subQ2,-1.0]])],"derivedFrom":subQ1}),-1.0]])]});}
            var Q3;
            {var subQ0=sQuery(id+"F28.wireOp",EDGE,"E162.0");Q3=makeQuery(id+"F28.imprint","IMPRINT",FACE,{"disambiguationData":[TD([[makeQuery(id+"F28.imprint","IMPRINT",EDGE,{"derivedFrom":subQ0}),1.0]])]});}
            var Q4;
            {var subQ0=sQuery(id+"F28.wireOp",EDGE,"E161.0");Q4=makeQuery(id+"F28.imprint","IMPRINT",FACE,{"disambiguationData":[TD([[makeQuery(id+"F28.imprint","IMPRINT",EDGE,{"derivedFrom":subQ0}),-1.0]])]});}
            var Q5;
            {var subQ0=sQuery(id+"F28.wireOp",EDGE,"E170.0");var subQ1=sQuery(id+"F28.wireOp",EDGE,"E167.0");var subQ2=makeQuery(id+"F28.imprint","INTERSECT",VERTEX,{"derivedFrom":[subQ1,subQ0]});Q5=makeQuery(id+"F28.imprint","IMPRINT",FACE,{"disambiguationData":[TD([[makeQuery(id+"F28.imprint","IMPRINT",EDGE,{"disambiguationData":[TD([[subQ2,-1.0]])],"derivedFrom":subQ1}),1.0]])]});}
            var Q6;
            {var subQ0=sQuery(id+"F28.wireOp",EDGE,"E171.0");var subQ1=sQuery(id+"F28.wireOp",EDGE,"E167.0");var subQ2=makeQuery(id+"F28.imprint","INTERSECT",VERTEX,{"derivedFrom":[subQ1,subQ0]});Q6=makeQuery(id+"F28.imprint","IMPRINT",FACE,{"disambiguationData":[TD([[makeQuery(id+"F28.imprint","IMPRINT",EDGE,{"disambiguationData":[TD([[subQ2,-1.0]])],"derivedFrom":subQ1}),1.0]])]});}
            var Q7;
            {var subQ0=sQuery(id+"F28.wireOp",EDGE,"E173.0");var subQ1=sQuery(id+"F28.wireOp",EDGE,"E167.0");var subQ2=makeQuery(id+"F28.imprint","INTERSECT",VERTEX,{"derivedFrom":[subQ1,subQ0]});Q7=makeQuery(id+"F28.imprint","IMPRINT",FACE,{"disambiguationData":[TD([[makeQuery(id+"F28.imprint","IMPRINT",EDGE,{"disambiguationData":[TD([[subQ2,-1.0]])],"derivedFrom":subQ1}),1.0]])]});}
            var Q8;
            {var subQ0=sQuery(id+"F28.wireOp",EDGE,"E179.0");Q8=makeQuery(id+"F28.imprint","IMPRINT",FACE,{"disambiguationData":[TD([[makeQuery(id+"F28.imprint","IMPRINT",EDGE,{"derivedFrom":subQ0}),1.0]])]});}
            var Q9;
            {var subQ0=sQuery(id+"F28.wireOp",EDGE,"E178.0");Q9=makeQuery(id+"F28.imprint","IMPRINT",FACE,{"disambiguationData":[TD([[makeQuery(id+"F28.imprint","IMPRINT",EDGE,{"derivedFrom":subQ0}),-1.0]])]});}
            extrude(context, id + "F29", {"entities" : qUnion([Q0, Q1, Q2, Q3, Q4, Q5, Q6, Q7, Q8, Q9]), "oppositeDirection" : true, "depth" : 18 * mm, "offsetDistance" : 25 * mm});
        }
        {
            var Q0;
            Q0=makeQuery(id+"F1.opExtrude","SWEPT_FACE",FACE,{"disambiguationData":[OSD([sQuery(id+"F0.wireOp",EDGE,"E4")])]});
            var sketch = newSketch(context, id + "F30", { "sketchPlane" : qUnion([Q0])});
            skLineSegment(sketch, "E180.0", {"start": v(0, 2198) * mm, "end": v(0, 2) * mm});
            skLineSegment(sketch, "E181.0", {"start": v(-2, 0) * mm, "end": v(-738, 0) * mm});
            skLineSegment(sketch, "E182", {"start": v(0, 60) * mm, "end": v(-740, 60) * mm});
            skLineSegment(sketch, "E183", {"start": v(-2, 0) * mm, "end": v(0, 0) * mm});
            skLineSegment(sketch, "E184", {"start": v(0, 0) * mm, "end": v(0, 2) * mm});
            skLineSegment(sketch, "E185", {"start": v(-42, 0) * mm, "end": v(-42, 60) * mm});
            skSolve(sketch);
        }
        {
            var Q0;
            Q0 = qSketchRegion(id + "F30", true);
            var Q1;
            Q1=makeQuery(id+"F1.opExtrude","SWEPT_FACE",FACE,{"disambiguationData":[OSD([sQuery(id+"F0.wireOp",EDGE,"E0.right")])]});
            extrude(context, id + "F31", {"entities" : qUnion([Q0]), "operationType" : NewBodyOperationType.REMOVE, "endBound" : BoundingType.UP_TO_SURFACE, "oppositeDirection" : true, "depth" : 25 * mm, "endBoundEntityFace" : qUnion([Q1]), "offsetDistance" : 25 * mm});
        }
        {
            var Q0;
            Q0=makeQuery(id+"F5.opExtrude","SWEPT_FACE",FACE,{"disambiguationData":[OSD([sQuery(id+"F0.wireOp",EDGE,"E2")])]});
            var sketch = newSketch(context, id + "F32", { "sketchPlane" : qUnion([Q0])});
            skLineSegment(sketch, "E186", {"start": v(42, 60) * mm, "end": v(42, 0) * mm});
            skLineSegment(sketch, "E187.0", {"start": v(0, 0) * mm, "end": v(0, 2180) * mm});
            skLineSegment(sketch, "E188.0", {"start": v(650, 0) * mm, "end": v(0, 0) * mm});
            skLineSegment(sketch, "E189", {"start": v(740, 60) * mm, "end": v(0, 60) * mm});
            skSolve(sketch);
        }
        {
            var Q0;
            Q0 = qSketchRegion(id + "F32", true);
            var Q1;
            Q1=makeQuery(id+"F5.opExtrude","SWEPT_FACE",FACE,{"disambiguationData":[OSD([sQuery(id+"F0.wireOp",EDGE,"E5")])]});
            extrude(context, id + "F33", {"entities" : qUnion([Q0]), "operationType" : NewBodyOperationType.REMOVE, "endBound" : BoundingType.UP_TO_SURFACE, "oppositeDirection" : true, "depth" : 25 * mm, "endBoundEntityFace" : qUnion([Q1]), "offsetDistance" : 25 * mm});
        }
        {
            var Q0;
            Q0=makeQuery(id+"F1.opExtrude","SWEPT_FACE",FACE,{"disambiguationData":[OSD([sQuery(id+"F0.wireOp",EDGE,"E4")])]});
            var sketch = newSketch(context, id + "F34", { "sketchPlane" : qUnion([Q0])});
            skLineSegment(sketch, "E190", {"start": v(-67.17, 1625.47) * mm, "end": v(-717.17, 1625.47) * mm});
            skLineSegment(sketch, "E191", {"start": v(-717.17, 1625.47) * mm, "end": v(-717.17, 1585.47) * mm});
            skLineSegment(sketch, "E192", {"start": v(-717.17, 1585.47) * mm, "end": v(-67.17, 1585.47) * mm});
            skLineSegment(sketch, "E193", {"start": v(-67.17, 1585.47) * mm, "end": v(-67.17, 1625.47) * mm});
            skSolve(sketch);
        }
        {
            var Q0;
            Q0=makeQuery(id+"F34.imprint","IMPRINT",FACE,{"disambiguationData":[TD([[makeQuery(id+"F34.imprint","IMPRINT",EDGE,{"derivedFrom":sQuery(id+"F34.wireOp",EDGE,"E190")}),1.0]])]});
            extrude(context, id + "F35", {"entities" : qUnion([Q0]), "depth" : 10 * mm, "offsetDistance" : 25 * mm});
        }
    });
